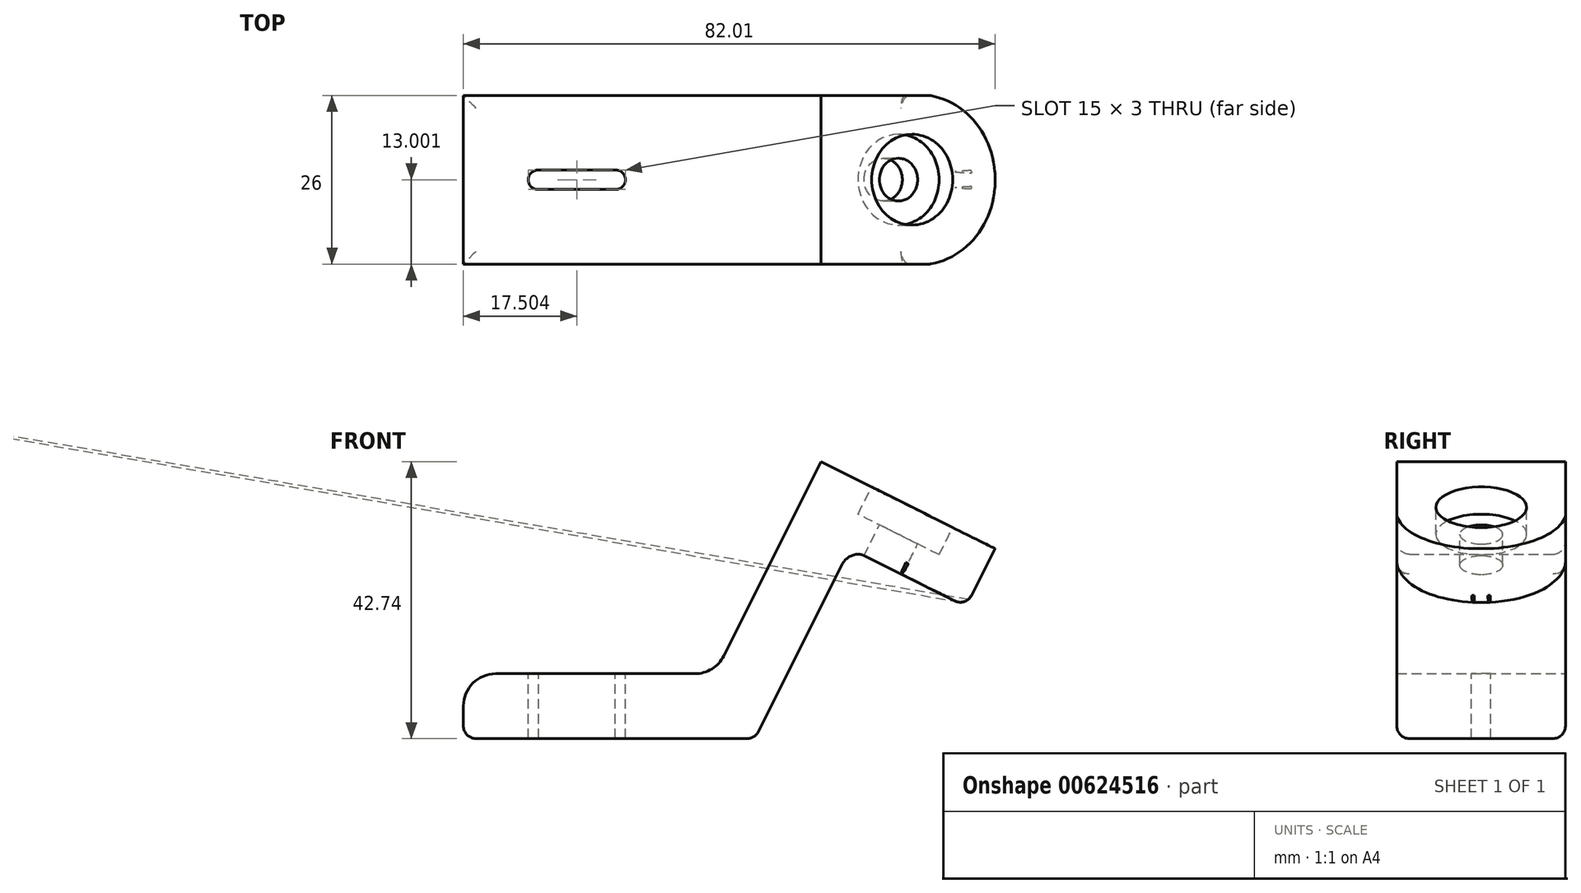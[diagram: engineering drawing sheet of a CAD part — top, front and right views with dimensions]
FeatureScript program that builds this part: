
annotation { "Feature Type Name" : "Feature", "Feature Type Description" : "" }
export const myFeature = defineFeature(function(context is Context, id is Id, definition is map)
    precondition{}
    {
        {
            var Q0;
            Q0=qCreatedBy(makeId("Front.planeOp"),FACE);
            var sketch = newSketch(context, id + "F0", { "sketchPlane" : qUnion([Q0])});
            skLineSegment(sketch, "E0", {"start": v(13.85, 6.71) * mm, "end": v(30.22, 39.45) * mm});
            skLineSegment(sketch, "E1", {"start": v(30.22, 39.45) * mm, "end": v(57.06, 26.03) * mm});
            skLineSegment(sketch, "E2", {"start": v(-24.95, 6.71) * mm, "end": v(-24.95, -3.29) * mm});
            skLineSegment(sketch, "E3", {"start": v(-24.95, -3.29) * mm, "end": v(13.85, -3.29) * mm});
            skLineSegment(sketch, "E4", {"start": v(57.06, 26.03) * mm, "end": v(52.58, 17.09) * mm});
            skLineSegment(sketch, "E5", {"start": v(-24.95, 6.71) * mm, "end": v(13.85, 6.71) * mm});
            skLineSegment(sketch, "E6", {"start": v(20.03, -3.29) * mm, "end": v(13.85, -3.29) * mm});
            skLineSegment(sketch, "E7", {"start": v(20.03, -3.29) * mm, "end": v(33.45, 23.54) * mm});
            skLineSegment(sketch, "E8", {"start": v(52.58, 17.09) * mm, "end": v(36.48, 25.14) * mm});
            skArc(sketch, "E9", {"start": v(33.45, 23.54) * mm, "mid": v(34.71, 24.83) * mm, "end": v(36.48, 25.14) * mm});
            skSolve(sketch);
        }
        {
            var Q0;
            Q0 = qSketchRegion(id + "F0", true);
            extrude(context, id + "F1", {"entities" : qUnion([Q0]), "depth" : 26 * mm, "offsetDistance" : 25 * mm});
        }
        {
            var Q0;
            Q0=makeQuery(id+"F1.opExtrude","SWEPT_FACE",FACE,{"disambiguationData":[OSD([sQuery(id+"F0.wireOp",EDGE,"E5")])]});
            var sketch = newSketch(context, id + "F2", { "sketchPlane" : qUnion([Q0])});
            skCircle(sketch, "E10", {"center": v(-13.45, -13) * mm, "radius": 1.5 * mm});
            skPoint(sketch, "E10.centerSnap0", {"position": v(-24.95, -13) * mm});
            skCircle(sketch, "E11", {"center": v(-1.45, -13) * mm, "radius": 1.5 * mm});
            skLineSegment(sketch, "E12", {"start": v(-13.55, -11.5) * mm, "end": v(-1.45, -11.5) * mm});
            skLineSegment(sketch, "E13", {"start": v(-13.37, -14.5) * mm, "end": v(-1.37, -14.5) * mm});
            skSolve(sketch);
        }
        {
            var Q0;
            Q0 = qSketchRegion(id + "F2", true);
            extrude(context, id + "F3", {"entities" : qUnion([Q0]), "operationType" : NewBodyOperationType.REMOVE, "oppositeDirection" : true, "depth" : 25 * mm, "offsetDistance" : 25 * mm});
        }
        {
            var Q0;
            Q0=makeQuery(id+"F1.opExtrude","SWEPT_EDGE",EDGE,{"disambiguationData":[OSD([sQuery(id+"F0.wireOp",EDGE,"E2"),sQuery(id+"F0.wireOp",EDGE,"E5")])]});
            fillet(context, id + "F4", {"entities" : qUnion([Q0]), "radius" : 5 * mm, "tangentPropagation" : true, "allowEdgeOverflow" : false});
        }
        {
            var Q0;
            Q0=makeQuery(id+"F1.opExtrude","SWEPT_EDGE",EDGE,{"disambiguationData":[OSD([sQuery(id+"F0.wireOp",EDGE,"E0"),sQuery(id+"F0.wireOp",EDGE,"E5")])]});
            fillet(context, id + "F5", {"entities" : qUnion([Q0]), "radius" : 5 * mm, "tangentPropagation" : true, "allowEdgeOverflow" : false});
        }
        {
            var Q0;
            Q0=makeQuery(id+"F1.opExtrude","CAP_EDGE",EDGE,{"disambiguationData":[OSD([sQuery(id+"F0.wireOp",EDGE,"E3"),sQuery(id+"F0.wireOp",EDGE,"E6")])],"isStart":false});
            var Q1;
            Q1=makeQuery(id+"F1.opExtrude","SWEPT_EDGE",EDGE,{"disambiguationData":[OSD([sQuery(id+"F0.wireOp",EDGE,"E2"),sQuery(id+"F0.wireOp",EDGE,"E3")])]});
            var Q2;
            Q2=makeQuery(id+"F1.opExtrude","CAP_EDGE",EDGE,{"disambiguationData":[OSD([sQuery(id+"F0.wireOp",EDGE,"E3"),sQuery(id+"F0.wireOp",EDGE,"E6")])],"isStart":true});
            var Q3;
            Q3=makeQuery(id+"F1.opExtrude","CAP_EDGE",EDGE,{"disambiguationData":[OSD([sQuery(id+"F0.wireOp",EDGE,"E7")])],"isStart":false});
            var Q4;
            Q4=makeQuery(id+"F1.opExtrude","CAP_EDGE",EDGE,{"disambiguationData":[OSD([sQuery(id+"F0.wireOp",EDGE,"E7")])],"isStart":true});
            var Q5;
            Q5=makeQuery(id+"F1.opExtrude","SWEPT_EDGE",EDGE,{"disambiguationData":[OSD([sQuery(id+"F0.wireOp",EDGE,"E6"),sQuery(id+"F0.wireOp",EDGE,"E7")])]});
            var Q6;
            Q6=makeQuery(id+"F1.opExtrude","CAP_EDGE",EDGE,{"disambiguationData":[OSD([sQuery(id+"F0.wireOp",EDGE,"E8")])],"isStart":false});
            var Q7;
            Q7=makeQuery(id+"F1.opExtrude","SWEPT_EDGE",EDGE,{"disambiguationData":[OSD([sQuery(id+"F0.wireOp",EDGE,"E4"),sQuery(id+"F0.wireOp",EDGE,"E8")])]});
            var Q8;
            Q8=makeQuery(id+"F1.opExtrude","SWEPT_FACE",FACE,{"disambiguationData":[OSD([sQuery(id+"F0.wireOp",EDGE,"E8")])]});
            fillet(context, id + "F6", {"entities" : qUnion([Q0, Q1, Q2, Q3, Q4, Q5, Q6, Q7, Q8]), "radius" : 1.93 * mm, "tangentPropagation" : true, "allowEdgeOverflow" : false});
        }
        {
            var Q0;
            Q0=makeQuery(id+"F1.opExtrude","SWEPT_FACE",FACE,{"disambiguationData":[OSD([sQuery(id+"F0.wireOp",EDGE,"E1")])]});
            var sketch = newSketch(context, id + "F7", { "sketchPlane" : qUnion([Q0])});
            skArc(sketch, "E14", {"start": v(24.4, -26) * mm, "mid": v(39.44, -13) * mm, "end": v(24.4, 0) * mm});
            skLineSegment(sketch, "E15", {"start": v(24.4, -26) * mm, "end": v(40.72, -28.4) * mm});
            skLineSegment(sketch, "E16", {"start": v(40.72, -28.4) * mm, "end": v(44.82, -20.08) * mm});
            skLineSegment(sketch, "E17", {"start": v(44.82, -20.08) * mm, "end": v(41.69, 3.9) * mm});
            skLineSegment(sketch, "E18", {"start": v(41.69, 3.9) * mm, "end": v(24.4, 0) * mm});
            skSolve(sketch);
        }
        {
            var Q0;
            Q0 = qSketchRegion(id + "F7", true);
            extrude(context, id + "F8", {"entities" : qUnion([Q0]), "operationType" : NewBodyOperationType.REMOVE, "oppositeDirection" : true, "depth" : 25 * mm, "offsetDistance" : 25 * mm});
        }
        {
            var Q0;
            Q0=makeQuery(id+"F1.opExtrude","SWEPT_FACE",FACE,{"disambiguationData":[OSD([sQuery(id+"F0.wireOp",EDGE,"E1")])]});
            var sketch = newSketch(context, id + "F9", { "sketchPlane" : qUnion([Q0])});
            skCircle(sketch, "E19", {"center": v(25.11, -12.97) * mm, "radius": 7 * mm});
            skSolve(sketch);
        }
        {
            var Q0;
            Q0 = qSketchRegion(id + "F9", true);
            extrude(context, id + "F10", {"entities" : qUnion([Q0]), "operationType" : NewBodyOperationType.REMOVE, "oppositeDirection" : true, "depth" : 4.7 * mm, "offsetDistance" : 25 * mm});
        }
        {
            var Q0;
            Q0=makeQuery(id+"F10.boolean.opBoolean","COPY",FACE,{"derivedFrom":makeQuery(id+"F10.opExtrude","CAP_FACE",FACE,{"disambiguationData":[OSD([sQuery(id+"F9.wireOp",EDGE,"E19")])],"isStart":false})});
            var sketch = newSketch(context, id + "F11", { "sketchPlane" : qUnion([Q0])});
            skCircle(sketch, "E20", {"center": v(25.11, -12.97) * mm, "radius": 3.3 * mm});
            skSolve(sketch);
        }
        {
            var Q0;
            Q0 = qSketchRegion(id + "F11", true);
            extrude(context, id + "F12", {"entities" : qUnion([Q0]), "operationType" : NewBodyOperationType.REMOVE, "endBound" : BoundingType.THROUGH_ALL, "oppositeDirection" : true, "depth" : 25 * mm, "offsetDistance" : 25 * mm});
        }
        {
            var Q0;
            Q0=makeQuery(id+"F8.boolean.opBoolean","INTERSECT",EDGE,{"disambiguationData":[OD(1.0)],"derivedFrom":[makeQuery(id+"F1.opExtrude","SWEPT_FACE",FACE,{"disambiguationData":[OSD([sQuery(id+"F0.wireOp",EDGE,"E8")])]}),makeQuery(id+"F8.opExtrude","SWEPT_FACE",FACE,{"disambiguationData":[OSD([sQuery(id+"F7.wireOp",EDGE,"E14")])]})]});
            var Q1;
            Q1=makeQuery(id+"F8.boolean.opBoolean","INTERSECT",EDGE,{"disambiguationData":[OD(0.0)],"derivedFrom":[makeQuery(id+"F1.opExtrude","SWEPT_FACE",FACE,{"disambiguationData":[OSD([sQuery(id+"F0.wireOp",EDGE,"E8")])]}),makeQuery(id+"F8.opExtrude","SWEPT_FACE",FACE,{"disambiguationData":[OSD([sQuery(id+"F7.wireOp",EDGE,"E14")])]})]});
            var Q2;
            Q2=makeQuery(id+"F8.boolean.opBoolean","INTERSECT",EDGE,{"derivedFrom":[makeQuery(id+"F6.opFillet","BLEND_FACE",FACE,{"disambiguationData":[OSD([sQuery(id+"F0.wireOp",EDGE,"E4"),sQuery(id+"F0.wireOp",EDGE,"E8")])]}),makeQuery(id+"F8.opExtrude","SWEPT_FACE",FACE,{"disambiguationData":[OSD([sQuery(id+"F7.wireOp",EDGE,"E14")])]})]});
            fillet(context, id + "F13", {"entities" : qUnion([Q0, Q1, Q2]), "radius" : 1.91 * mm, "tangentPropagation" : true, "allowEdgeOverflow" : false});
        }
    });
